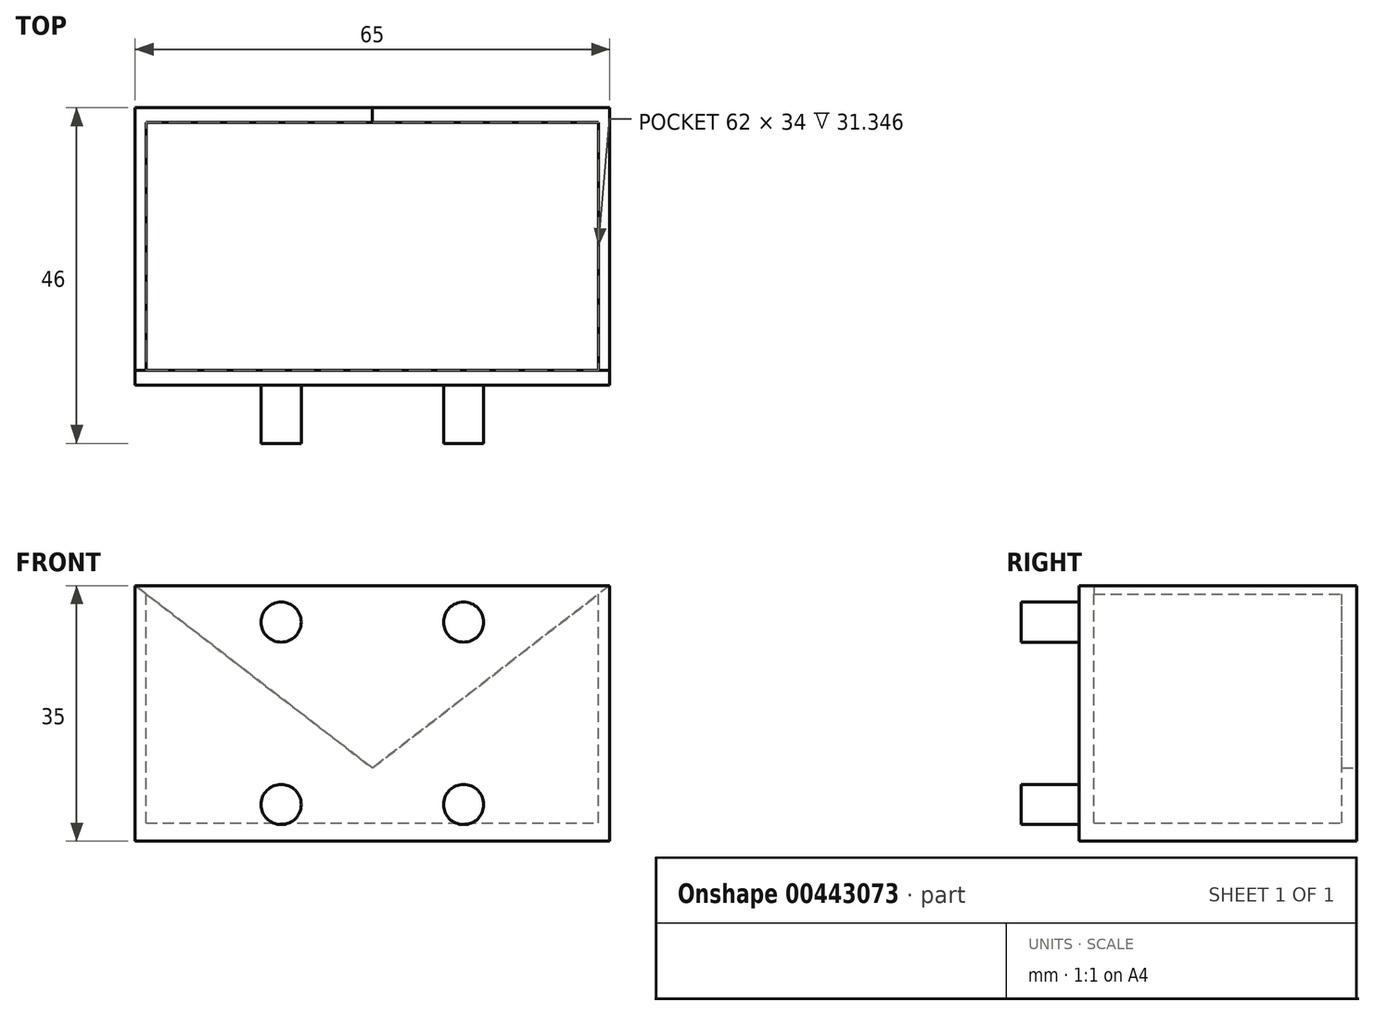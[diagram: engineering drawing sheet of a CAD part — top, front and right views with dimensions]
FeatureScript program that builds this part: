
annotation { "Feature Type Name" : "Feature", "Feature Type Description" : "" }
export const myFeature = defineFeature(function(context is Context, id is Id, definition is map)
    precondition{}
    {
        {
            var Q0;
            Q0=qCreatedBy(makeId("Top.planeOp"),FACE);
            var sketch = newSketch(context, id + "F0", { "sketchPlane" : qUnion([Q0])});
            skLineSegment(sketch, "E0.bottom", {"start": v(32.5, -19) * mm, "end": v(-32.5, -19) * mm});
            skLineSegment(sketch, "E0.top", {"start": v(32.5, 19) * mm, "end": v(-32.5, 19) * mm});
            skLineSegment(sketch, "E0.left", {"start": v(32.5, -19) * mm, "end": v(32.5, 19) * mm});
            skLineSegment(sketch, "E0.right", {"start": v(-32.5, -19) * mm, "end": v(-32.5, 19) * mm});
            skPoint(sketch, "E0.middle", {"position": v(0, 0) * mm});
            skSolve(sketch);
        }
        {
            var Q0;
            Q0 = qSketchRegion(id + "F0", true);
            extrude(context, id + "F1", {"entities" : qUnion([Q0]), "depth" : 35 * mm});
        }
        {
            var Q0;
            Q0=makeQuery(id+"F1.opExtrude","CAP_FACE",FACE,{"disambiguationData":[OSD([sQuery(id+"F0.wireOp",EDGE,"E0.bottom"),sQuery(id+"F0.wireOp",EDGE,"E0.top"),sQuery(id+"F0.wireOp",EDGE,"E0.left"),sQuery(id+"F0.wireOp",EDGE,"E0.right")])],"isStart":false});
            var sketch = newSketch(context, id + "F2", { "sketchPlane" : qUnion([Q0])});
            skLineSegment(sketch, "E1.bottom", {"start": v(-31, -17) * mm, "end": v(31, -17) * mm});
            skLineSegment(sketch, "E1.top", {"start": v(-31, 17) * mm, "end": v(31, 17) * mm});
            skLineSegment(sketch, "E1.left", {"start": v(-31, -17) * mm, "end": v(-31, 17) * mm});
            skLineSegment(sketch, "E1.right", {"start": v(31, -17) * mm, "end": v(31, 17) * mm});
            skPoint(sketch, "E1.middle", {"position": v(0, 0) * mm});
            skSolve(sketch);
        }
        {
            var Q0;
            Q0 = qSketchRegion(id + "F2", true);
            extrude(context, id + "F3", {"entities" : qUnion([Q0]), "operationType" : NewBodyOperationType.REMOVE, "oppositeDirection" : true, "depth" : 32.5 * mm});
        }
        {
            var Q0;
            Q0=makeQuery(id+"F1.opExtrude","SWEPT_FACE",FACE,{"disambiguationData":[OSD([sQuery(id+"F0.wireOp",EDGE,"E0.bottom")])]});
            var sketch = newSketch(context, id + "F4", { "sketchPlane" : qUnion([Q0])});
            skCircle(sketch, "E2", {"center": v(-12.5, 5) * mm, "radius": 2.75 * mm});
            skCircle(sketch, "E3", {"center": v(-12.5, 30) * mm, "radius": 2.75 * mm});
            skCircle(sketch, "E4.MirrorC", {"center": v(12.5, 30) * mm, "radius": 2.75 * mm});
            skCircle(sketch, "E5.MirrorC", {"center": v(12.5, 5) * mm, "radius": 2.75 * mm});
            skSolve(sketch);
        }
        {
            var Q0;
            Q0 = qSketchRegion(id + "F4", true);
            extrude(context, id + "F5", {"entities" : qUnion([Q0]), "operationType" : NewBodyOperationType.ADD, "depth" : 8 * mm});
        }
        {
            var Q0;
            Q0=makeQuery(id+"F1.opExtrude","SWEPT_FACE",FACE,{"disambiguationData":[OSD([sQuery(id+"F0.wireOp",EDGE,"E0.top")])]});
            var sketch = newSketch(context, id + "F6", { "sketchPlane" : qUnion([Q0])});
            skLineSegment(sketch, "E6", {"start": v(-32.5, 35) * mm, "end": v(0, 10) * mm});
            skPoint(sketch, "E6.endSnap0", {"position": v(0, 35) * mm});
            skLineSegment(sketch, "E7", {"start": v(0, 10) * mm, "end": v(32.5, 35) * mm});
            skLineSegment(sketch, "E8", {"start": v(32.5, 35) * mm, "end": v(-32.5, 35) * mm});
            skSolve(sketch);
        }
        {
            var Q0;
            Q0 = qSketchRegion(id + "F6", true);
            var Q1;
            Q1=makeQuery(id+"F3.boolean.opBoolean","COPY",FACE,{"derivedFrom":makeQuery(id+"F3.opExtrude","SWEPT_FACE",FACE,{"disambiguationData":[OSD([sQuery(id+"F2.wireOp",EDGE,"E1.bottom")])]})});
            extrude(context, id + "F7", {"entities" : qUnion([Q0]), "operationType" : NewBodyOperationType.REMOVE, "endBound" : BoundingType.UP_TO_SURFACE, "oppositeDirection" : true, "endBoundEntityFace" : qUnion([Q1]), "depth" : 25 * mm});
        }
    });
